# Revit family: Fireplace_Gas_HeatNGlo_Villa-Gas
name_source: partatom
category: Mechanical Equipment
revit_build: Autodesk Revit 2015 (Build: 20140323_1530(x64)
units: mm (PartAtom-declared; Revit-internal decimal feet)

## types (4) — shared parameters
Assembly Code = D3020
Construction Details = http://www.arcat.com
Default Elevation = 0' - 0"
Description = Heat & Glo Gas Burning Outdoor Fireplace - Villa Gas as Specified
Efficiency Ratings = as Specified
Fixture Finish = Metal - HeatNGlo - Metallic Black
Fuel Consumption = as Specified
HVAC_BTU Output = 0.0 Btu/h
Heating Capacity = as Specified
Keynote = 10305
Manufacturer = Heat & Glo
Manufacturer Website = http://www.heatnglo.com
Opening Height = 1' - 8"
Product Data = http://www.arcat.com
Revision = R2_2014-11
Sales Information = http://www.heatnglo.com
Send Message = http://www.arcat.com
Specification = http://www.arcat.com
Standards Conformance = as Specified
URL = http://www.heatnglo.com
Unit Depth = 1' - 11"
Unit Height = 3' - 6 3/8"
zero-valued in all types: Expected Lifespan (Years), Maintenance Schedule (Months), Warranty Duration (Years)

## per-type parameters (varying)
| type | Fuel Type | HVAC_BTU Input | Model | Opening Width | Rear Width | Unit Weight | Unit Width |
| 42x30 Viewing Area LP | LP | 42000.0 Btu/h | ODVILLAG-42 | 3' - 6" | 2' - 5 3/4" | 260 | 3' - 11 1/8" |
| 42x30 Viewing Area NG | NG | 42000.0 Btu/h | ODVILLAG-42 | 3' - 6" | 2' - 5 3/4" | 260 | 3' - 11 1/8" |
| 36x24 Viewing Area LP | LP | 40000.0 Btu/h | ODVILLAG-36 | 3' - 0" | 1' - 11 3/4" | 240 | 3' - 5 1/8" |
| 36x24 Viewing Area NG | NG | 40000.0 Btu/h | ODVILLAG-36 | 3' - 0" | 1' - 11 3/4" | 240 | 3' - 5 1/8" |

## geometry (parser evidence)
native form markers: Blend x12, Sweep x3
no freeform markers — native parametric forms only
